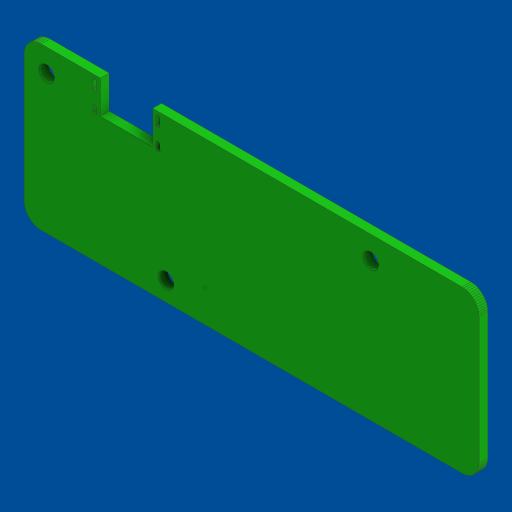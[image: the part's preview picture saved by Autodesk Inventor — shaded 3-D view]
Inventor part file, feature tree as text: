
AUTODESK INVENTOR PART (.ipt)
format: ipt  version: 2023.2 (Build 272271000, 271)  size: 313,856 bytes
history: native  units: mm
features: extrude x1, sketch x1
ambient origin geometry x8: Origin, YZ Plane, XZ Plane, XY Plane, X Axis, Y Axis, Z Axis, Center Point
bodies: Solid1 (feature_tree)
feature tree (2):
  extrude  "Extrusion1"  [1 undecoded]
  sketch  "Sketch1"  dims[d0=1.55mm d1=0.0mm]
note: 1 required parameter value undecoded (feature->parameter linkage not recoverable at this tier; creation-order binding heuristic only, values carry confidence <= 0.55)
